# Revit family: Horno HLF 940 SS
name_source: partatom
category: Specialty Equipment
revit_build: Autodesk Revit 2017 (Build: 20160225_1515(x64)
units: mm (PartAtom-declared; Revit-internal decimal feet)

## family parameters
Always vertical = Yes
Cut with Voids When Loaded = No
Part Type = Normal
Room Calculation Point = No
Round Connector Dimension = Use Diameter
Shared = No
Work Plane-Based = No

## types (2) — shared parameters
Ancho = 89 cm
Ca_2_Iluminación Interior = 2 x 25W
Ca_2_Motor Refrigeración = 18 W
Ca_2_Resistencia Inferior = 1055 W
Ca_2_Turbo Multifunción = 30
Ca_3_Display Digital = No
Ca_3_Guías laterales cromadas = Yes
Ca_3_Mandos Pop Up = No
Ca_3_Programador - Touch Control = Yes
Ca_3_Salida de vahos integrada = Bóveda
Ca_3_Ventilación Tangencial con optimización de salida = Yes
Ca_4_Anti-vuelco de parrillas = Yes
Ca_4_Protector del grill = Yes
Ca_4_Termostato de seguridad = Yes
Ca_5_Acero Inox Anti-huella = Yes
Ca_5_Esmalte Crystal Clean = No
Ca_5_Esmalte Hydroclean™ = Yes
Ca_6_Asa para extracción de bandejas = No
Ca_6_Asador rotativo = No
Ca_6_Bandeja de asados profunda 50mm = 1
Ca_6_Bandeja modular con tapa de cristal = No
Ca_6_Parrilla reforzada de asados-cromada = 1
Ca_Alto = 48 cm
Ca_Alto Interior = 32 cm
Ca_Ancho = 89 cm
Ca_Ancho Interior = 61.5 cm
Ca_Certificaciones = Certificado Aprobación SEC
Ca_Clase de Eficiencia Energética = A
Ca_Creado por = Catálogo Arquitectura
Ca_Código Catálogo Arquitectura = 465_TEK_008
Ca_Código EAN = 8421152155042
Ca_Código del Producto = 41592223
Ca_Especificaciones Técnicas = Horno eléctrico multifunción empotrable para muebles de cocina modelo HLF 940 SS
Ca_Fabricante = Teka
Ca_Instalación = Empotrado
Ca_Itemizado CDT = E 08 06 02
Ca_Masterformat = 11 30 13.13
Ca_Material Principal = Acero Inoxidable Antihuella+Cristal Templado
Ca_Medidas de embalaje = 65x63.5x65.5
Ca_País de Fabricación = España
Ca_Peso = 58 kg
Ca_Producto = Horno HLF 940 SS
Ca_Profundidad = 56 cm
Ca_Profundidad Interior = 39.5 cm
Ca_Representante = Teka Chile
Ca_Teléfono = 99821 1017
Ca_Usos = Horno eléctrico multifunción empotrable para muebles de cocina
Ca_Web del Fabricante = www.teka.com
Ca_Web del Representante = www.tekaindustrial.com/cl
Description = Horno eléctrico multifunción empotrable para muebles de cocina
Fondo = 56 cm
Interior Negro = Teka_Interior Negro
Logo Teka = Teka_Logo
Manufacturer = Teka
Model = HLF 940 SS
Panel Interior = Teka_Panel Interior
Panel Negro = Teka_Panel Negro
Panel Vidrio = Teka_Panel Vidrio
Perilla Negro = Teka_Perilla Negro
URL = www.teka.com
Voltage = 220-240

## per-type parameters (varying)
| type | Alto | Ancho Encastre | Borde Aluminio | Ca_1_Cable de conexión | Ca_1_Potencia nominal max. W. | Ca_2_Resistencia Grill: Normal/Maxi-Grill | Ca_2_Resistencia Turbo | Ca_2_Resistencia superior + inferior | Ca_3_N° de Funciones de cocinado | Ca_4_Bloqueo de seguridad del panel | Ca_4_Cristal Puerta | Ca_4_Desconexión automática en puerta | Ca_6_Bandeja Pastelera | Ca_Capacidad en Litros | Perilla Aluminio | Wattage |
| Horno HLF 940 SS | 47.067 cm | 84.4 cm | Teka_Acero Inox | 190 cm | 3553 | 1050/1700 | 2400 W | 2105 W | 9 | Yes | 3 | Yes | Yes | 77 | Teka_Acero Inox | 3553 |
| Horno HS 900 | 48 cm | 86 cm | Teka_Aluminio | 110 cm | 2848 | 1700/2750 | 0 W | 2550 W | 7 | No | 2 | No | No | 91 | Teka_Perilla Aluminio | 2848 |

## geometry (parser evidence)
native form markers: Sweep x2
no freeform markers — native parametric forms only
